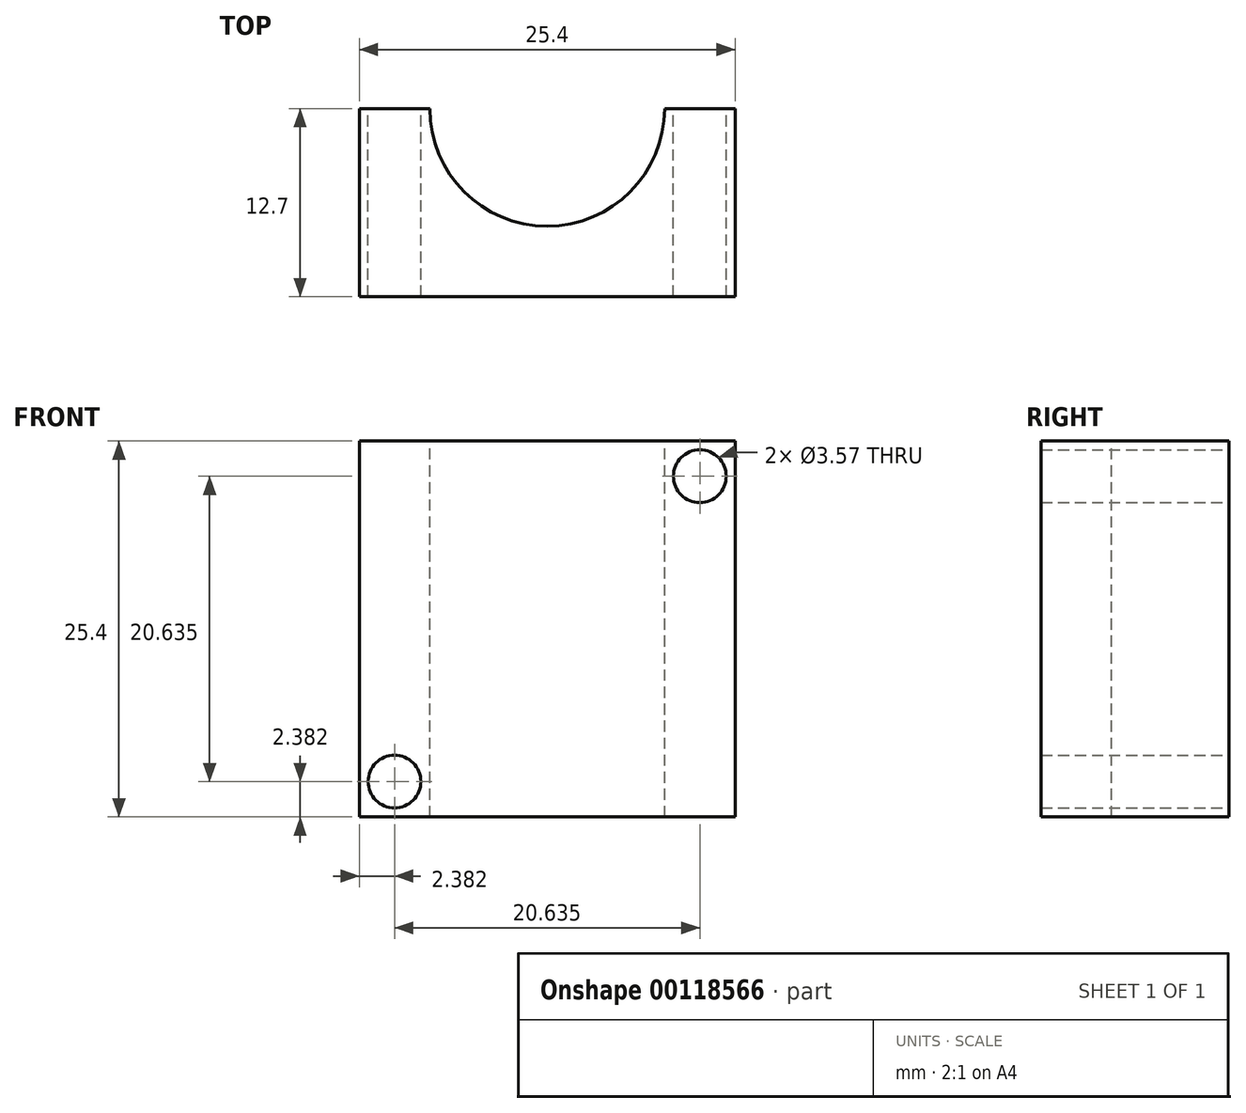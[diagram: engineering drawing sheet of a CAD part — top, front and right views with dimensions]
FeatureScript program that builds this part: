
annotation { "Feature Type Name" : "Feature", "Feature Type Description" : "" }
export const myFeature = defineFeature(function(context is Context, id is Id, definition is map)
    precondition{}
    {
        {
            var Q0;
            Q0=qCreatedBy(makeId("Front.planeOp"),FACE);
            var sketch = newSketch(context, id + "F0", { "sketchPlane" : qUnion([Q0])});
            skLineSegment(sketch, "E0.bottom", {"start": v(12.7, 12.7) * mm, "end": v(-12.7, 12.7) * mm});
            skLineSegment(sketch, "E0.top", {"start": v(12.7, -12.7) * mm, "end": v(-12.7, -12.7) * mm});
            skLineSegment(sketch, "E0.left", {"start": v(12.7, 12.7) * mm, "end": v(12.7, -12.7) * mm});
            skLineSegment(sketch, "E0.right", {"start": v(-12.7, 12.7) * mm, "end": v(-12.7, -12.7) * mm});
            skPoint(sketch, "E0.middle", {"position": v(0, 0) * mm});
            skSolve(sketch);
        }
        {
            var Q0;
            Q0 = qSketchRegion(id + "F0", true);
            extrude(context, id + "F1", {"entities" : qUnion([Q0]), "depth" : 12.7 * mm});
        }
        {
            var Q0;
            Q0=makeQuery(id+"F1.opExtrude","SWEPT_FACE",FACE,{"disambiguationData":[OSD([sQuery(id+"F0.wireOp",EDGE,"E0.bottom")])]});
            var sketch = newSketch(context, id + "F2", { "sketchPlane" : qUnion([Q0])});
            skCircle(sketch, "E1", {"center": v(0, 0) * mm, "radius": 7.94 * mm});
            skSolve(sketch);
        }
        {
            var Q0;
            {var subQ0=sQuery(id+"F2.wireOp",EDGE,"E1");var subQ1=makeQuery(id+"F1.opExtrude","CAP_EDGE",EDGE,{"disambiguationData":[OSD([sQuery(id+"F0.wireOp",EDGE,"E0.bottom")])],"isStart":true});var subQ2=makeQuery(id+"F2.imprint","INTERSECT",VERTEX,{"disambiguationData":[OD(0.0)],"derivedFrom":[subQ1,subQ0]});Q0=makeQuery(id+"F2.imprint","IMPRINT",FACE,{"disambiguationData":[TD([[makeQuery(id+"F2.imprint","IMPRINT",EDGE,{"disambiguationData":[TD([[subQ2,-1.0]])],"derivedFrom":subQ0}),1.0]])]});}
            var Q1;
            {var subQ0=sQuery(id+"F2.wireOp",EDGE,"E1");var subQ1=makeQuery(id+"F1.opExtrude","CAP_EDGE",EDGE,{"disambiguationData":[OSD([sQuery(id+"F0.wireOp",EDGE,"E0.bottom")])],"isStart":true});var subQ2=makeQuery(id+"F2.imprint","INTERSECT",VERTEX,{"disambiguationData":[OD(0.0)],"derivedFrom":[subQ1,subQ0]});Q1=makeQuery(id+"F2.imprint","IMPRINT",FACE,{"disambiguationData":[TD([[makeQuery(id+"F2.imprint","IMPRINT",EDGE,{"disambiguationData":[TD([[subQ2,1.0]])],"derivedFrom":subQ0}),1.0]])]});}
            extrude(context, id + "F3", {"entities" : qUnion([Q0, Q1]), "operationType" : NewBodyOperationType.REMOVE, "endBound" : BoundingType.THROUGH_ALL, "oppositeDirection" : true, "depth" : 25.4 * mm});
        }
        {
            var Q0;
            Q0=qCreatedBy(makeId("Front.planeOp"),FACE);
            var sketch = newSketch(context, id + "F4", { "sketchPlane" : qUnion([Q0])});
            skCircle(sketch, "E2", {"center": v(10.32, 10.32) * mm, "radius": 1.78 * mm});
            skCircle(sketch, "E3.MirrorC", {"center": v(-10.32, 10.32) * mm, "radius": 1.78 * mm});
            skCircle(sketch, "E4.MirrorC", {"center": v(-10.32, -10.32) * mm, "radius": 1.78 * mm});
            skCircle(sketch, "E5.MirrorC", {"center": v(10.32, -10.32) * mm, "radius": 1.78 * mm});
            skSolve(sketch);
        }
        {
            var Q0;
            Q0=makeQuery(id+"F4.imprint","IMPRINT",FACE,{"disambiguationData":[TD([[makeQuery(id+"F4.imprint","IMPRINT",EDGE,{"derivedFrom":sQuery(id+"F4.wireOp",EDGE,"E3.MirrorC")}),-1.0]])]});
            var Q1;
            Q1=makeQuery(id+"F4.imprint","IMPRINT",FACE,{"disambiguationData":[TD([[makeQuery(id+"F4.imprint","IMPRINT",EDGE,{"derivedFrom":sQuery(id+"F4.wireOp",EDGE,"E4.MirrorC")}),1.0]])]});
            var Q2;
            Q2=makeQuery(id+"F4.imprint","IMPRINT",FACE,{"disambiguationData":[TD([[makeQuery(id+"F4.imprint","IMPRINT",EDGE,{"derivedFrom":sQuery(id+"F4.wireOp",EDGE,"E5.MirrorC")}),-1.0]])]});
            var Q3;
            Q3=makeQuery(id+"F4.imprint","IMPRINT",FACE,{"disambiguationData":[TD([[makeQuery(id+"F4.imprint","IMPRINT",EDGE,{"derivedFrom":sQuery(id+"F4.wireOp",EDGE,"E2")}),1.0]])]});
            extrude(context, id + "F5", {"entities" : qUnion([Q0, Q1, Q2, Q3]), "operationType" : NewBodyOperationType.REMOVE, "endBound" : BoundingType.THROUGH_ALL, "depth" : 25.4 * mm});
        }
    });
